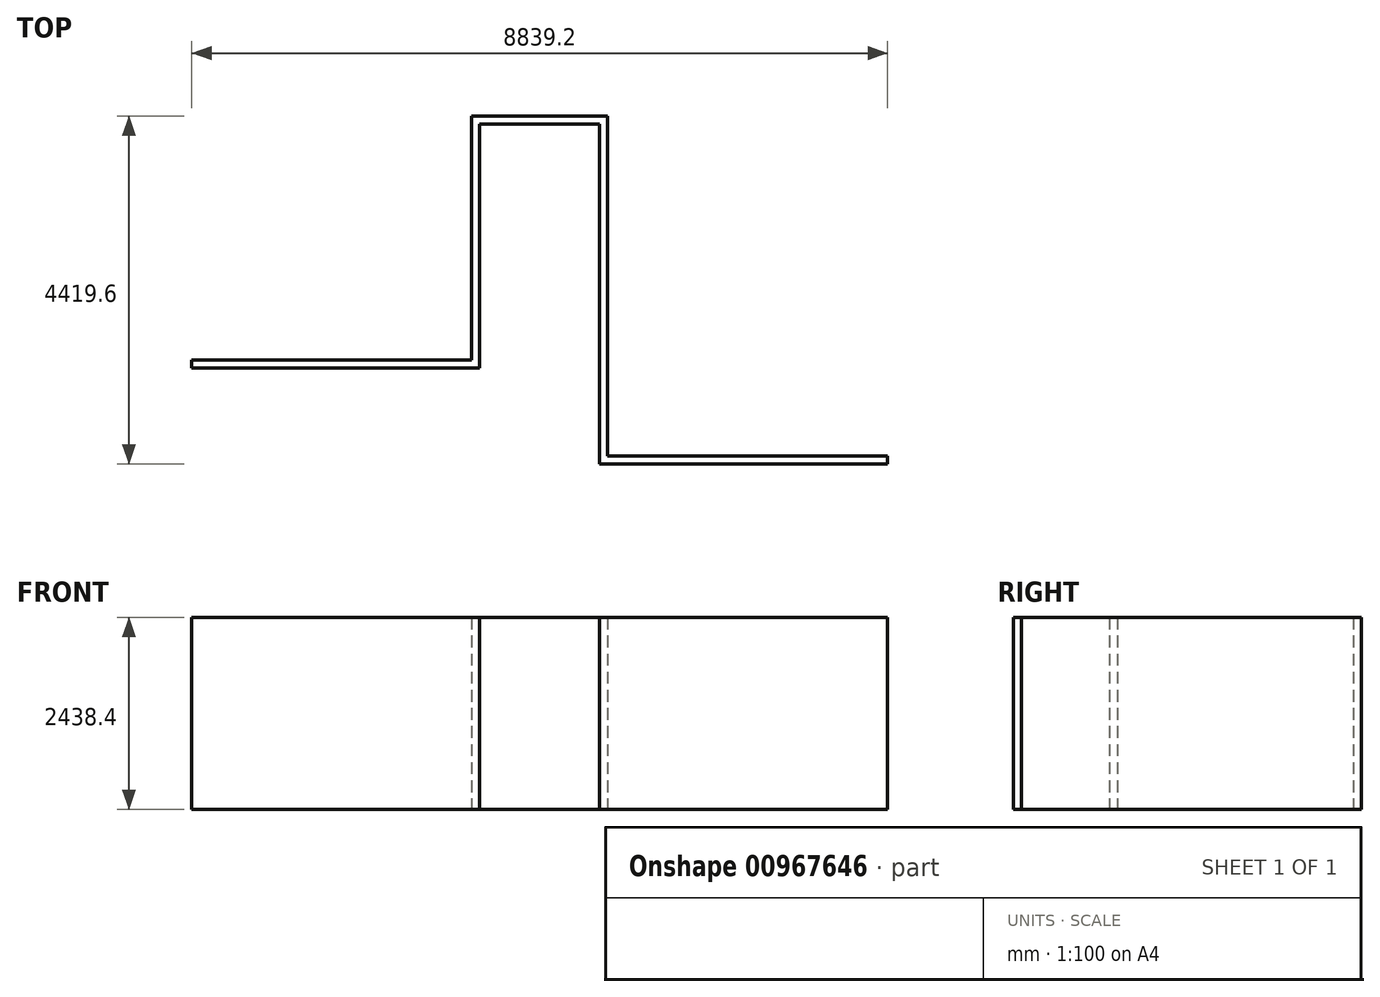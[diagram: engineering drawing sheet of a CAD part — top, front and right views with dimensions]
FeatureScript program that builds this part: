
annotation { "Feature Type Name" : "Feature", "Feature Type Description" : "" }
export const myFeature = defineFeature(function(context is Context, id is Id, definition is map)
    precondition{}
    {
        {
            var Q0;
            Q0=qCreatedBy(makeId("Top.planeOp"),FACE);
            var sketch = newSketch(context, id + "F0", { "sketchPlane" : qUnion([Q0])});
            skLineSegment(sketch, "E0.bottom", {"start": v(-4419.6, 3810) * mm, "end": v(4419.6, 3810) * mm, "construction": true});
            skLineSegment(sketch, "E0.top", {"start": v(-4419.6, -3810) * mm, "end": v(4419.6, -3810) * mm, "construction": true});
            skLineSegment(sketch, "E0.left", {"start": v(-4419.6, 3810) * mm, "end": v(-4419.6, -3810) * mm, "construction": true});
            skLineSegment(sketch, "E0.right", {"start": v(4419.6, 3810) * mm, "end": v(4419.6, -3810) * mm, "construction": true});
            skPoint(sketch, "E0.middle", {"position": v(0, 0) * mm});
            skLineSegment(sketch, "E1", {"start": v(4419.6, -609.6) * mm, "end": v(762, -609.6) * mm});
            skLineSegment(sketch, "E2", {"start": v(762, -609.6) * mm, "end": v(762, 3708.4) * mm});
            skLineSegment(sketch, "E3", {"start": v(762, 3810) * mm, "end": v(863.6, 3810) * mm});
            skLineSegment(sketch, "E4", {"start": v(863.6, 3810) * mm, "end": v(863.6, -508) * mm});
            skLineSegment(sketch, "E5", {"start": v(863.6, -508) * mm, "end": v(4419.6, -508) * mm});
            skLineSegment(sketch, "E6", {"start": v(4419.6, -508) * mm, "end": v(4419.6, -609.6) * mm});
            skLineSegment(sketch, "E7", {"start": v(863.6, -508) * mm, "end": v(762, -508) * mm, "construction": true});
            skLineSegment(sketch, "E8", {"start": v(863.6, -508) * mm, "end": v(863.6, -609.6) * mm, "construction": true});
            skLineSegment(sketch, "E9", {"start": v(-4419.6, 609.6) * mm, "end": v(-762, 609.6) * mm});
            skLineSegment(sketch, "E10", {"start": v(-762, 609.6) * mm, "end": v(-762, 3708.4) * mm});
            skLineSegment(sketch, "E11", {"start": v(-762, 3810) * mm, "end": v(-863.6, 3810) * mm});
            skLineSegment(sketch, "E12", {"start": v(-863.6, 3810) * mm, "end": v(-863.6, 711.2) * mm});
            skLineSegment(sketch, "E13", {"start": v(-863.6, 711.2) * mm, "end": v(-4419.6, 711.2) * mm});
            skLineSegment(sketch, "E14", {"start": v(-4419.6, 711.2) * mm, "end": v(-4419.6, 609.6) * mm});
            skLineSegment(sketch, "E15", {"start": v(-863.6, 711.2) * mm, "end": v(-863.6, 609.6) * mm, "construction": true});
            skLineSegment(sketch, "E16", {"start": v(-863.6, 711.2) * mm, "end": v(-762, 711.2) * mm, "construction": true});
            skLineSegment(sketch, "E17", {"start": v(-762, 3810) * mm, "end": v(762, 3810) * mm});
            skLineSegment(sketch, "E18", {"start": v(-762, 3708.4) * mm, "end": v(762, 3708.4) * mm});
            skLineSegment(sketch, "E19", {"start": v(-762, 3708.4) * mm, "end": v(-762, 3810) * mm, "construction": true});
            skSolve(sketch);
        }
        {
            var Q0;
            Q0 = qSketchRegion(id + "F0", true);
            extrude(context, id + "F1", {"entities" : qUnion([Q0]), "depth" : 2438.4 * mm, "offsetDistance" : 30.48 * mm});
        }
    });
